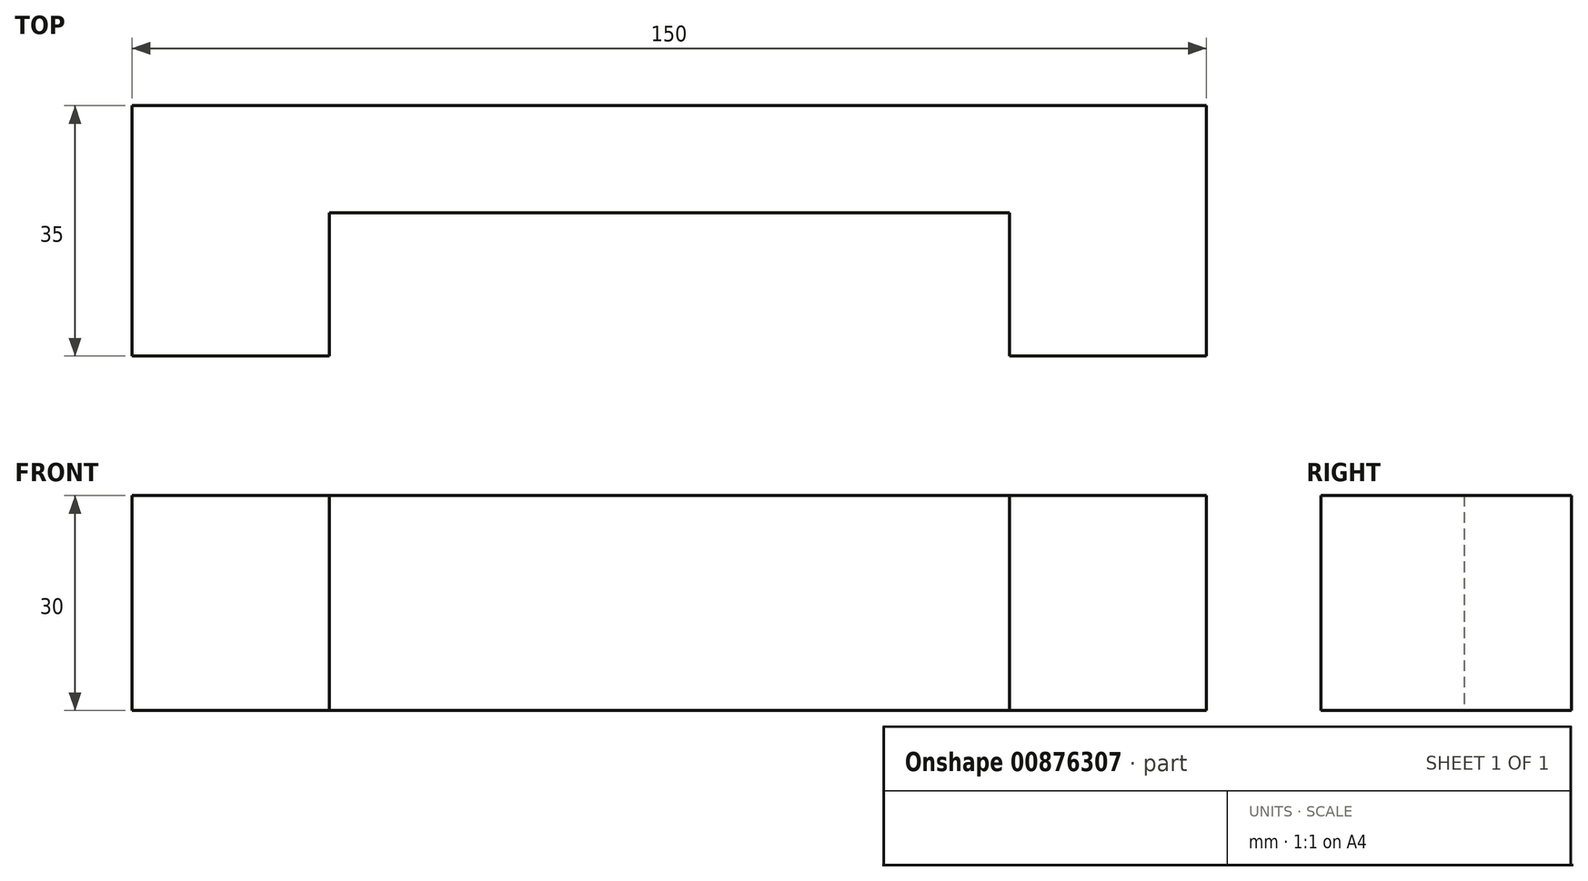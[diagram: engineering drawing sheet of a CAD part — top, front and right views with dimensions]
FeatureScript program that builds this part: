
annotation { "Feature Type Name" : "Feature", "Feature Type Description" : "" }
export const myFeature = defineFeature(function(context is Context, id is Id, definition is map)
    precondition{}
    {
        {
            var Q0;
            Q0=qCreatedBy(makeId("Top.planeOp"),FACE);
            var sketch = newSketch(context, id + "F0", { "sketchPlane" : qUnion([Q0])});
            skLineSegment(sketch, "E0.bottom", {"start": v(0, 0) * mm, "end": v(27.5, 0) * mm});
            skLineSegment(sketch, "E0.top", {"start": v(0, 35) * mm, "end": v(150, 35) * mm});
            skLineSegment(sketch, "E0.left", {"start": v(0, 0) * mm, "end": v(0, 35) * mm});
            skLineSegment(sketch, "E0.right", {"start": v(150, 0) * mm, "end": v(150, 35) * mm});
            skLineSegment(sketch, "E1.top", {"start": v(27.5, 20) * mm, "end": v(122.5, 20) * mm});
            skLineSegment(sketch, "E1.left", {"start": v(27.5, 0) * mm, "end": v(27.5, 20) * mm});
            skLineSegment(sketch, "E1.right", {"start": v(122.5, 0) * mm, "end": v(122.5, 20) * mm});
            skLineSegment(sketch, "E2.trimOffspring", {"start": v(122.5, 0) * mm, "end": v(150, 0) * mm});
            skSolve(sketch);
        }
        {
            var Q0;
            Q0 = qSketchRegion(id + "F0", true);
            extrude(context, id + "F1", {"entities" : qUnion([Q0]), "depth" : 30 * mm, "offsetDistance" : 25.4 * mm});
        }
    });
